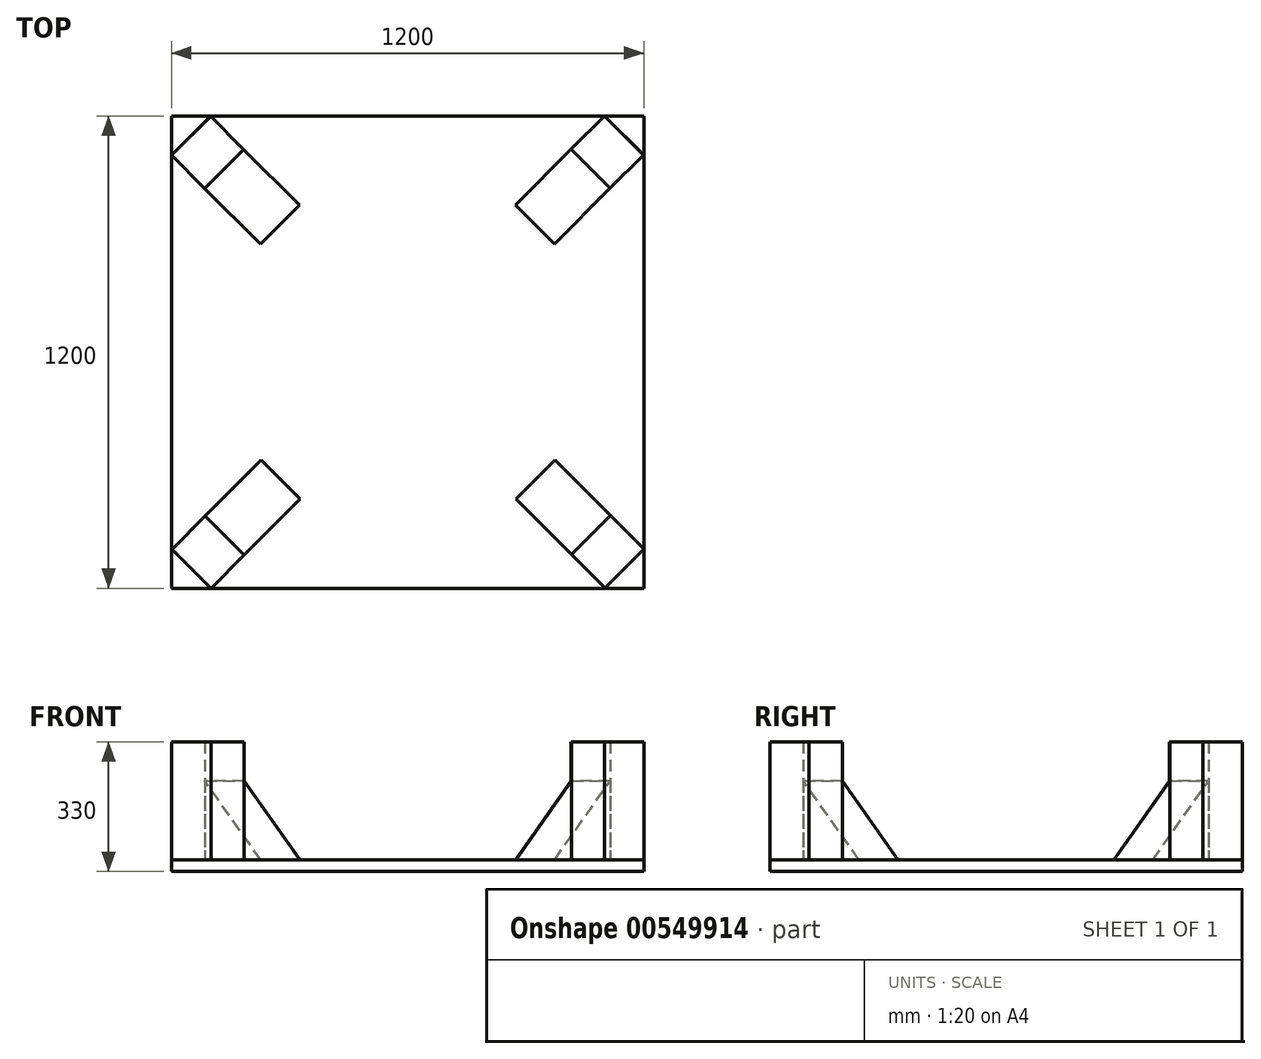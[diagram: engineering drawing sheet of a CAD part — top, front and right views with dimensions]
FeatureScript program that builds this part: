
annotation { "Feature Type Name" : "Feature", "Feature Type Description" : "" }
export const myFeature = defineFeature(function(context is Context, id is Id, definition is map)
    precondition{}
    {
        {
            var Q0;
            Q0=qCreatedBy(makeId("Top.planeOp"),FACE);
            var sketch = newSketch(context, id + "F0", { "sketchPlane" : qUnion([Q0])});
            skLineSegment(sketch, "E0", {"start": v(0, 600) * mm, "end": v(0, -600) * mm, "construction": true});
            skLineSegment(sketch, "E1", {"start": v(-600, 0) * mm, "end": v(600, 0) * mm, "construction": true});
            skLineSegment(sketch, "E2", {"start": v(-600, 600) * mm, "end": v(-600, -600) * mm});
            skLineSegment(sketch, "E3", {"start": v(-600, 600) * mm, "end": v(600, 600) * mm});
            skLineSegment(sketch, "E4", {"start": v(600, 600) * mm, "end": v(600, -600) * mm});
            skLineSegment(sketch, "E5", {"start": v(-600, -600) * mm, "end": v(600, -600) * mm});
            skSolve(sketch);
        }
        {
            var Q0;
            Q0=makeQuery(id+"F0.imprint","IMPRINT",FACE,{"disambiguationData":[TD([[makeQuery(id+"F0.imprint","IMPRINT",EDGE,{"derivedFrom":sQuery(id+"F0.wireOp",EDGE,"E2")}),1.0]])]});
            extrude(context, id + "F1", {"entities" : qUnion([Q0]), "oppositeDirection" : true, "depth" : 30 * mm, "offsetDistance" : 25 * mm});
        }
        {
            var Q0;
            Q0=makeQuery(id+"F1.opExtrude","CAP_FACE",FACE,{"disambiguationData":[OSD([sQuery(id+"F0.wireOp",EDGE,"E2"),sQuery(id+"F0.wireOp",EDGE,"E3"),sQuery(id+"F0.wireOp",EDGE,"E4"),sQuery(id+"F0.wireOp",EDGE,"E5")])],"isStart":true});
            var sketch = newSketch(context, id + "F2", { "sketchPlane" : qUnion([Q0])});
            skLineSegment(sketch, "E6", {"start": v(-600, -600) * mm, "end": v(-500, -600) * mm});
            skLineSegment(sketch, "E7", {"start": v(-500, -600) * mm, "end": v(-600, -500) * mm});
            skLineSegment(sketch, "E8", {"start": v(-600, -500) * mm, "end": v(-600, -600) * mm});
            skSolve(sketch);
        }
        {
            var Q0;
            Q0=makeQuery(id+"F2.imprint","IMPRINT",FACE,{"disambiguationData":[TD([[makeQuery(id+"F2.imprint","IMPRINT",EDGE,{"derivedFrom":sQuery(id+"F2.wireOp",EDGE,"E6")}),1.0]])]});
            extrude(context, id + "F3", {"entities" : qUnion([Q0]), "depth" : 300 * mm, "offsetDistance" : 25 * mm});
        }
        {
            var Q0;
            Q0=makeQuery(id+"F3.opExtrude","SWEPT_EDGE",EDGE,{"disambiguationData":[OSD([sQuery(id+"F0.wireOp",EDGE,"E5"),sQuery(id+"F2.wireOp",EDGE,"E6"),sQuery(id+"F2.wireOp",EDGE,"E7")])]});
            cPoint(context, id + "F4", {"entities" : qUnion([Q0]), "parameter" : 0.5});
        }
        {
            var Q0;
            Q0 = qCreatedBy(id + "F4" ,VERTEX);
            var Q1;
            Q1=makeQuery(id+"F3.opExtrude","CAP_EDGE",EDGE,{"disambiguationData":[OSD([sQuery(id+"F2.wireOp",EDGE,"E7")])],"isStart":true});
            cPlane(context, id + "F5", {"entities" : qUnion([Q0, Q1]), "cplaneType" : CPlaneType.LINE_POINT, "offset" : 25 * mm, "width" : 150 * mm, "height" : 150 * mm});
        }
        {
            var Q0;
            Q0=qCreatedBy(id+"F5.planeOp",FACE);
            var sketch = newSketch(context, id + "F6", { "sketchPlane" : qUnion([Q0])});
            skLineSegment(sketch, "E9.0", {"start": v(777.82, 300) * mm, "end": v(777.82, 0) * mm});
            skLineSegment(sketch, "E10.0", {"start": v(848.53, 0) * mm, "end": v(0, 0) * mm});
            skLineSegment(sketch, "E11", {"start": v(777.82, 200) * mm, "end": v(577.82, 0) * mm, "construction": true});
            skLineSegment(sketch, "E12", {"start": v(458, 0) * mm, "end": v(658, 200) * mm});
            skLineSegment(sketch, "E13", {"start": v(658, 200) * mm, "end": v(658, 0) * mm});
            skLineSegment(sketch, "E14.bottom", {"start": v(658, 200) * mm, "end": v(777.82, 200) * mm, "construction": true});
            skLineSegment(sketch, "E14.top", {"start": v(658, 0) * mm, "end": v(777.82, 0) * mm});
            skLineSegment(sketch, "E14.right", {"start": v(777.82, 200) * mm, "end": v(777.82, 0) * mm});
            skLineSegment(sketch, "E15", {"start": v(777.82, 300) * mm, "end": v(658, 300) * mm});
            skLineSegment(sketch, "E16", {"start": v(658, 300) * mm, "end": v(658, 200) * mm});
            skSolve(sketch);
        }
        {
            var Q0;
            {var subQ0=sQuery(id+"F6.wireOp",EDGE,"E12");Q0=makeQuery(id+"F6.imprint","IMPRINT",FACE,{"disambiguationData":[TD([[makeQuery(id+"F6.imprint","IMPRINT",EDGE,{"derivedFrom":subQ0}),-1.0]])]});}
            var Q1;
            Q1=makeQuery(id+"F3.opExtrude","SWEPT_FACE",FACE,{"disambiguationData":[OSD([sQuery(id+"F2.wireOp",EDGE,"E8")])]});
            extrude(context, id + "F7", {"entities" : qUnion([Q0]), "depth" : 140 * mm, "endBoundEntityFace" : qUnion([Q1]), "offsetDistance" : 25 * mm});
        }
        {
            var Q0;
            Q0=qCreatedBy(makeId("Front.planeOp"),FACE);
            var sketch = newSketch(context, id + "F8", { "sketchPlane" : qUnion([Q0])});
            skLineSegment(sketch, "E17", {"start": v(0, 0) * mm, "end": v(0, 300) * mm, "construction": true});
            skSolve(sketch);
        }
        {
            var Q0;
            Q0=makeQuery(id+"F7.opExtrude","SWEPT_BODY",BODY,{"disambiguationData":[OSD([sQuery(id+"F6.wireOp",EDGE,"E9.0"),sQuery(id+"F6.wireOp",EDGE,"E10.0"),sQuery(id+"F6.wireOp",EDGE,"E11")])]});
            var Q1;
            Q1=sQuery(id+"F8.wireOp",EDGE,"E17");
            transform(context, id + "F9", {"entities" : qUnion([Q0]), "transformType" : TransformType.ROTATION, "transformAxis" : qUnion([Q1]), "angle" : 180 * degree, "makeCopy" : true});
        }
        {
            var Q0;
            Q0=makeQuery(id+"F6.imprint","IMPRINT",FACE,{"disambiguationData":[TD([[makeQuery(id+"F6.imprint","IMPRINT",EDGE,{"derivedFrom":sQuery(id+"F6.wireOp",EDGE,"E9.0")}),-1.0]])]});
            extrude(context, id + "F10", {"entities" : qUnion([Q0]), "depth" : 140 * mm, "offsetDistance" : 25 * mm});
        }
        {
            var Q0;
            Q0=makeQuery(id+"F7.opExtrude","SWEPT_BODY",BODY,{"disambiguationData":[OSD([sQuery(id+"F6.wireOp",EDGE,"E10.0"),sQuery(id+"F6.wireOp",EDGE,"E12"),sQuery(id+"F6.wireOp",EDGE,"E13")])]});
            var Q1;
            Q1=sQuery(id+"F8.wireOp",EDGE,"E17");
            transform(context, id + "F11", {"entities" : qUnion([Q0]), "transformType" : TransformType.ROTATION, "transformAxis" : qUnion([Q1]), "angle" : 90 * degree, "makeCopy" : true});
        }
        {
            var Q0;
            Q0=makeQuery(id+"F7.opExtrude","SWEPT_BODY",BODY,{"disambiguationData":[OSD([sQuery(id+"F6.wireOp",EDGE,"E10.0"),sQuery(id+"F6.wireOp",EDGE,"E12"),sQuery(id+"F6.wireOp",EDGE,"E13")])]});
            var Q1;
            Q1=sQuery(id+"F8.wireOp",EDGE,"E17");
            transform(context, id + "F12", {"entities" : qUnion([Q0]), "transformType" : TransformType.ROTATION, "transformAxis" : qUnion([Q1]), "angle" : 270 * degree, "makeCopy" : true});
        }
        {
            var Q0;
            Q0=makeQuery(id+"F10.opExtrude","SWEPT_BODY",BODY,{"disambiguationData":[OSD([sQuery(id+"F6.wireOp",EDGE,"E9.0"),sQuery(id+"F6.wireOp",EDGE,"E14.top"),sQuery(id+"F6.wireOp",EDGE,"E13"),sQuery(id+"F6.wireOp",EDGE,"E14.right"),sQuery(id+"F6.wireOp",EDGE,"E15"),sQuery(id+"F6.wireOp",EDGE,"E16")])]});
            var Q1;
            Q1=sQuery(id+"F8.wireOp",EDGE,"E17");
            transform(context, id + "F13", {"entities" : qUnion([Q0]), "transformType" : TransformType.ROTATION, "transformAxis" : qUnion([Q1]), "angle" : 90 * degree, "makeCopy" : true});
        }
        {
            var Q0;
            Q0=makeQuery(id+"F10.opExtrude","SWEPT_BODY",BODY,{"disambiguationData":[OSD([sQuery(id+"F6.wireOp",EDGE,"E9.0"),sQuery(id+"F6.wireOp",EDGE,"E14.top"),sQuery(id+"F6.wireOp",EDGE,"E13"),sQuery(id+"F6.wireOp",EDGE,"E14.right"),sQuery(id+"F6.wireOp",EDGE,"E15"),sQuery(id+"F6.wireOp",EDGE,"E16")])]});
            var Q1;
            Q1=sQuery(id+"F8.wireOp",EDGE,"E17");
            transform(context, id + "F14", {"entities" : qUnion([Q0]), "transformType" : TransformType.ROTATION, "transformAxis" : qUnion([Q1]), "angle" : 180 * degree, "makeCopy" : true});
        }
        {
            var Q0;
            Q0=makeQuery(id+"F10.opExtrude","SWEPT_BODY",BODY,{"disambiguationData":[OSD([sQuery(id+"F6.wireOp",EDGE,"E9.0"),sQuery(id+"F6.wireOp",EDGE,"E14.top"),sQuery(id+"F6.wireOp",EDGE,"E13"),sQuery(id+"F6.wireOp",EDGE,"E14.right"),sQuery(id+"F6.wireOp",EDGE,"E15"),sQuery(id+"F6.wireOp",EDGE,"E16")])]});
            var Q1;
            Q1=sQuery(id+"F8.wireOp",EDGE,"E17");
            transform(context, id + "F15", {"entities" : qUnion([Q0]), "transformType" : TransformType.ROTATION, "transformAxis" : qUnion([Q1]), "angle" : 270 * degree, "makeCopy" : true});
        }
        {
            var Q0;
            Q0=makeQuery(id+"F3.opExtrude","SWEPT_BODY",BODY,{"disambiguationData":[OSD([sQuery(id+"F2.wireOp",EDGE,"E6"),sQuery(id+"F2.wireOp",EDGE,"E7"),sQuery(id+"F2.wireOp",EDGE,"E8")])]});
            var Q1;
            Q1=sQuery(id+"F8.wireOp",EDGE,"E17");
            transform(context, id + "F16", {"entities" : qUnion([Q0]), "transformType" : TransformType.ROTATION, "transformAxis" : qUnion([Q1]), "angle" : 90 * degree, "makeCopy" : true});
        }
        {
            var Q0;
            Q0=makeQuery(id+"F3.opExtrude","SWEPT_BODY",BODY,{"disambiguationData":[OSD([sQuery(id+"F2.wireOp",EDGE,"E6"),sQuery(id+"F2.wireOp",EDGE,"E7"),sQuery(id+"F2.wireOp",EDGE,"E8")])]});
            var Q1;
            Q1=sQuery(id+"F8.wireOp",EDGE,"E17");
            transform(context, id + "F17", {"entities" : qUnion([Q0]), "transformType" : TransformType.ROTATION, "transformAxis" : qUnion([Q1]), "angle" : 180 * degree, "makeCopy" : true});
        }
        {
            var Q0;
            Q0=makeQuery(id+"F3.opExtrude","SWEPT_BODY",BODY,{"disambiguationData":[OSD([sQuery(id+"F2.wireOp",EDGE,"E6"),sQuery(id+"F2.wireOp",EDGE,"E7"),sQuery(id+"F2.wireOp",EDGE,"E8")])]});
            var Q1;
            Q1=sQuery(id+"F8.wireOp",EDGE,"E17");
            transform(context, id + "F18", {"entities" : qUnion([Q0]), "transformType" : TransformType.ROTATION, "transformAxis" : qUnion([Q1]), "angle" : 270 * degree, "makeCopy" : true});
        }
    });
